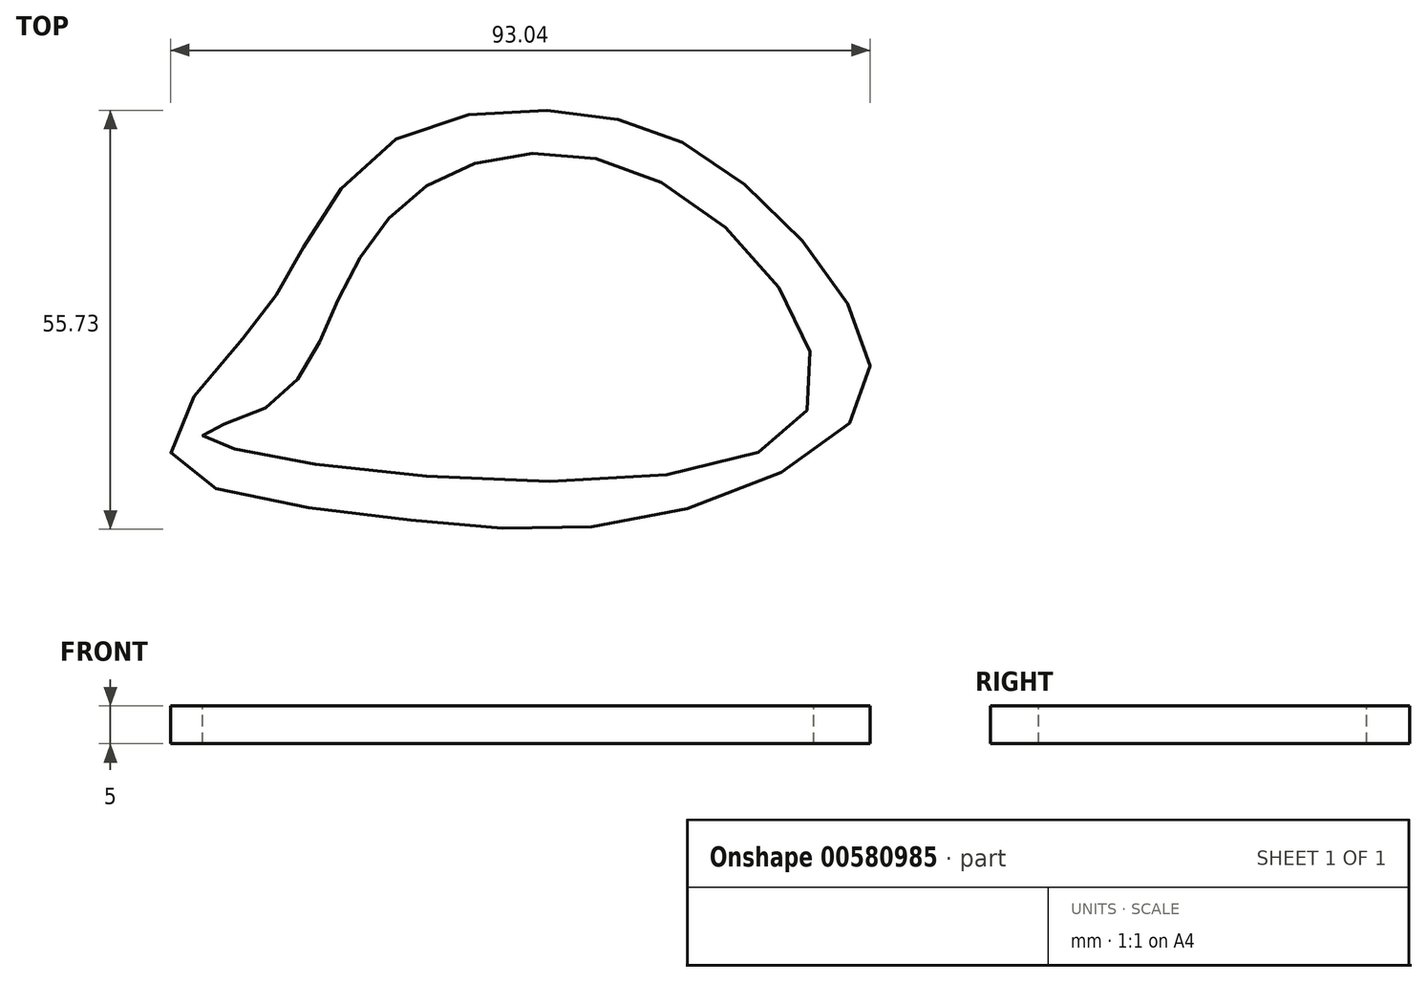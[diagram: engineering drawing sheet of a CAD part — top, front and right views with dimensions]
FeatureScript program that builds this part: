
annotation { "Feature Type Name" : "Feature", "Feature Type Description" : "" }
export const myFeature = defineFeature(function(context is Context, id is Id, definition is map)
    precondition{}
    {
        {
            var Q0;
            Q0=qCreatedBy(makeId("Top.planeOp"),FACE);
            var sketch = newSketch(context, id + "F0", { "sketchPlane" : qUnion([Q0])});
            skFitSpline(sketch, "E0", {"points": [v(-65.2, 11.76) * mm, v(-55.73, 25.8) * mm, v(-42.6, 41.99) * mm, v(-9.92, 40.16) * mm, v(4.12, 8.1) * mm, v(-73.44, 7.79) * mm, v(-65.2, 11.76) * mm]});
            skFitSpline(sketch, "E1", {"points": [v(-68.25, 20.92) * mm, v(-61.53, 30.7) * mm, v(-49.32, 46.57) * mm, v(-25.8, 51.15) * mm, v(-6.87, 45.35) * mm, v(11.15, 27.33) * mm, v(13.9, 11.76) * mm, v(-15.73, -3.2) * mm, v(-50.85, -2.6) * mm, v(-77.72, 5.34) * mm, v(-68.25, 20.92) * mm]});
            skSolve(sketch);
        }
        {
            var Q0;
            Q0=sQuery(id+"F0.wireOp",EDGE,"E1");
            var Q1;
            Q1=sQuery(id+"F0.wireOp",EDGE,"E0");
            extrude(context, id + "F1", {"bodyType" : ToolBodyType.SURFACE, "surfaceEntities" : qUnion([Q0, Q1]), "depth" : 5 * mm, "offsetDistance" : 25.4 * mm});
        }
    });
